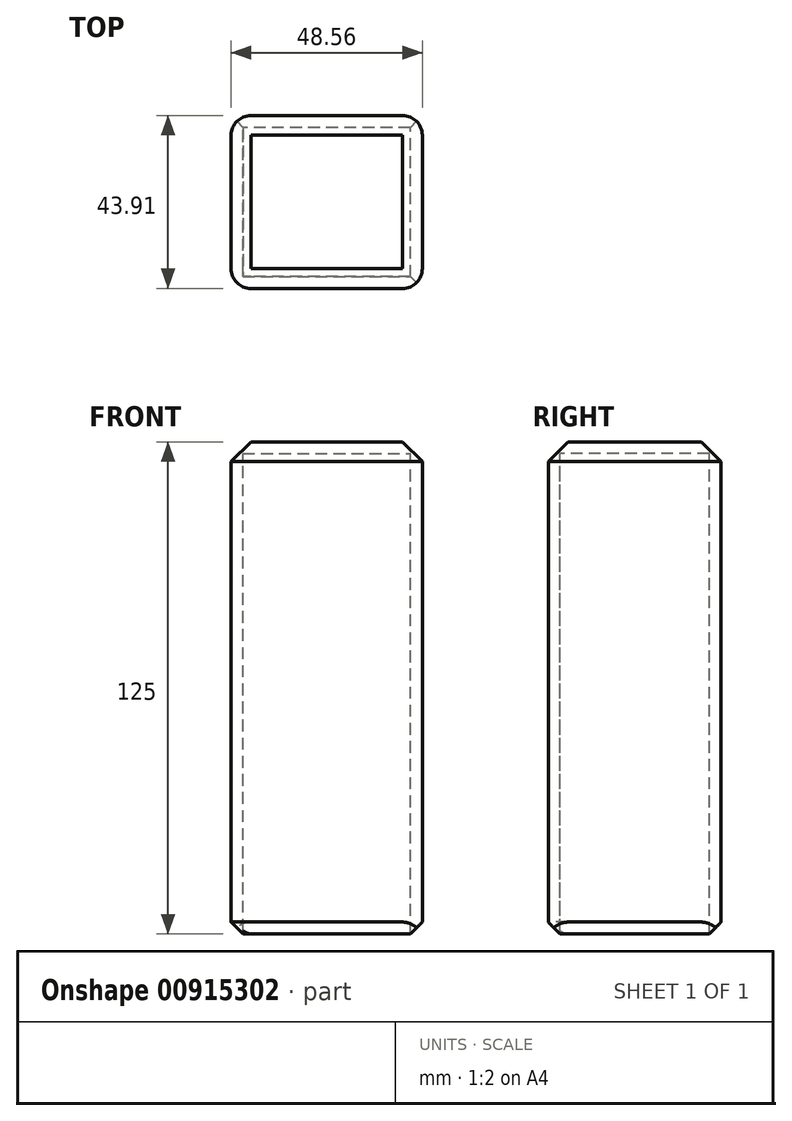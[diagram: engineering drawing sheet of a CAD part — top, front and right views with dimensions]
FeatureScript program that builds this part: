
annotation { "Feature Type Name" : "Feature", "Feature Type Description" : "" }
export const myFeature = defineFeature(function(context is Context, id is Id, definition is map)
    precondition{}
    {
        {
            var Q0;
            Q0=qCreatedBy(makeId("Top.planeOp"),FACE);
            var sketch = newSketch(context, id + "F0", { "sketchPlane" : qUnion([Q0])});
            skLineSegment(sketch, "E0.bottom", {"start": v(-10.36, 11.53) * mm, "end": v(38.2, 11.53) * mm});
            skLineSegment(sketch, "E0.top", {"start": v(-10.36, -32.38) * mm, "end": v(38.2, -32.38) * mm});
            skLineSegment(sketch, "E0.left", {"start": v(-10.36, 11.53) * mm, "end": v(-10.36, -32.38) * mm});
            skLineSegment(sketch, "E0.right", {"start": v(38.2, 11.53) * mm, "end": v(38.2, -32.38) * mm});
            skLineSegment(sketch, "E1.0", {"start": v(-7.36, 8.53) * mm, "end": v(35.2, 8.53) * mm});
            skLineSegment(sketch, "E1.1", {"start": v(-7.36, 8.53) * mm, "end": v(-7.36, -29.38) * mm});
            skLineSegment(sketch, "E1.2", {"start": v(-7.36, -29.38) * mm, "end": v(35.2, -29.38) * mm});
            skLineSegment(sketch, "E1.3", {"start": v(35.2, 8.53) * mm, "end": v(35.2, -29.38) * mm});
            skSolve(sketch);
        }
        {
            var Q0;
            Q0 = qSketchRegion(id + "F0", true);
            extrude(context, id + "F1", {"entities" : qUnion([Q0]), "oppositeDirection" : true, "depth" : 127 * mm, "offsetDistance" : 25 * mm});
        }
        {
            var Q0;
            Q0=makeQuery(id+"F0.imprint","IMPRINT",FACE,{"disambiguationData":[TD([[makeQuery(id+"F0.imprint","IMPRINT",EDGE,{"derivedFrom":sQuery(id+"F0.wireOp",EDGE,"E1.0")}),-1.0]])]});
            extrude(context, id + "F2", {"entities" : qUnion([Q0]), "operationType" : NewBodyOperationType.ADD, "oppositeDirection" : true, "depth" : 3 * mm, "offsetDistance" : 25 * mm});
        }
        {
            var Q0;
            Q0=makeQuery(id+"F1.opExtrude","SWEPT_EDGE",EDGE,{"disambiguationData":[OSD([sQuery(id+"F0.wireOp",EDGE,"E0.top"),sQuery(id+"F0.wireOp",EDGE,"E0.left")])]});
            fillet(context, id + "F3", {"entities" : qUnion([Q0]), "radius" : 5 * mm, "tangentPropagation" : true, "allowEdgeOverflow" : false});
        }
        {
            var Q0;
            Q0=makeQuery(id+"F1.opExtrude","CAP_EDGE",EDGE,{"disambiguationData":[OSD([sQuery(id+"F0.wireOp",EDGE,"E0.left")])],"isStart":false});
            var Q1;
            Q1=makeQuery(id+"F1.opExtrude","CAP_EDGE",EDGE,{"disambiguationData":[OSD([sQuery(id+"F0.wireOp",EDGE,"E0.right")])],"isStart":false});
            var Q2;
            Q2=makeQuery(id+"F1.opExtrude","CAP_EDGE",EDGE,{"disambiguationData":[OSD([sQuery(id+"F0.wireOp",EDGE,"E0.bottom")])],"isStart":false});
            chamfer(context, id + "F4", {"entities" : qUnion([Q0, Q1, Q2]), "width" : 5 * mm, "tangentPropagation" : true});
        }
        {
            var Q0;
            Q0=makeQuery(id+"F1.opExtrude","SWEPT_EDGE",EDGE,{"disambiguationData":[OSD([sQuery(id+"F0.wireOp",EDGE,"E0.bottom"),sQuery(id+"F0.wireOp",EDGE,"E0.left")])]});
            var Q1;
            Q1=makeQuery(id+"F1.opExtrude","SWEPT_EDGE",EDGE,{"disambiguationData":[OSD([sQuery(id+"F0.wireOp",EDGE,"E0.bottom"),sQuery(id+"F0.wireOp",EDGE,"E0.right")])]});
            var Q2;
            Q2=makeQuery(id+"F1.opExtrude","SWEPT_EDGE",EDGE,{"disambiguationData":[OSD([sQuery(id+"F0.wireOp",EDGE,"E0.top"),sQuery(id+"F0.wireOp",EDGE,"E0.right")])]});
            fillet(context, id + "F5", {"entities" : qUnion([Q0, Q1, Q2]), "radius" : 5 * mm, "tangentPropagation" : true, "allowEdgeOverflow" : false});
        }
        {
            var Q0;
            Q0=makeQuery(id+"F1.opExtrude","CAP_EDGE",EDGE,{"disambiguationData":[OSD([sQuery(id+"F0.wireOp",EDGE,"E0.top")])],"isStart":true});
            chamfer(context, id + "F6", {"entities" : qUnion([Q0]), "width" : 5 * mm, "tangentPropagation" : true});
        }
    });
